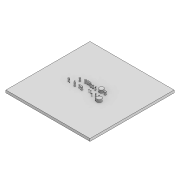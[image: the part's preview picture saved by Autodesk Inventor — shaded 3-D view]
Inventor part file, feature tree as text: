
AUTODESK INVENTOR PART (.ipt)
format: ipt  version: 2021 (Build 250183000, 183)  size: 325,120 bytes
history: native  units: in
note: dims shown in document units (in); Inventor stores cm internally (conversion verified against a paired STEP export)
features: sketch x7, extrude x6, projected_geometry x5, fillet x1
ambient origin geometry x8: Origin, YZ Plane, XZ Plane, XY Plane, X Axis, Y Axis, Z Axis, Center Point
bodies: Solid1 (feature_tree)
feature tree (19):
  extrude  "Extrusion1"  Depth=3937.0079in
  extrude  "Extrusion2"  Depth=118.1102in
  fillet  "Fillet1"  Radius=118.1102in
  extrude  "Extrusion3"  Depth=118.1102in TaperAngle=0.0deg
  extrude  "Extrusion4"  TaperAngle=0.0deg  [1 undecoded]
  sketch  "Sketch5"  dims[d14=118.1102in d15=0.0in]
  extrude  "Extrusion5"  [1 undecoded]
  extrude  "Extrusion6"  [1 undecoded]
  sketch  "Sketch1"  dims[d0=3937.0079in d1=3937.0079in]
  sketch  "Sketch2"  dims[d2=118.1102in d3=0.0in d4=157.4803in d5=118.1102in d6=0.0in]
  projected_geometry  "Projected Loop1"
  sketch  "Sketch3"  dims[d7=19.685in d8=118.1102in d9=0.0in]
  projected_geometry  "Projected Loop2"
  sketch  "Sketch4"  dims[d10=1.0in d11=0.0in d12=0.0in d13=0.0in]
  projected_geometry  "Projected Loop3"
  projected_geometry  "Projected Loop4"
  sketch  "Sketch6"
  projected_geometry  "Projected Loop5"
  sketch  "Sketch7"
note: 3 required parameter values undecoded (feature->parameter linkage not recoverable at this tier; creation-order binding heuristic only, values carry confidence <= 0.55)
